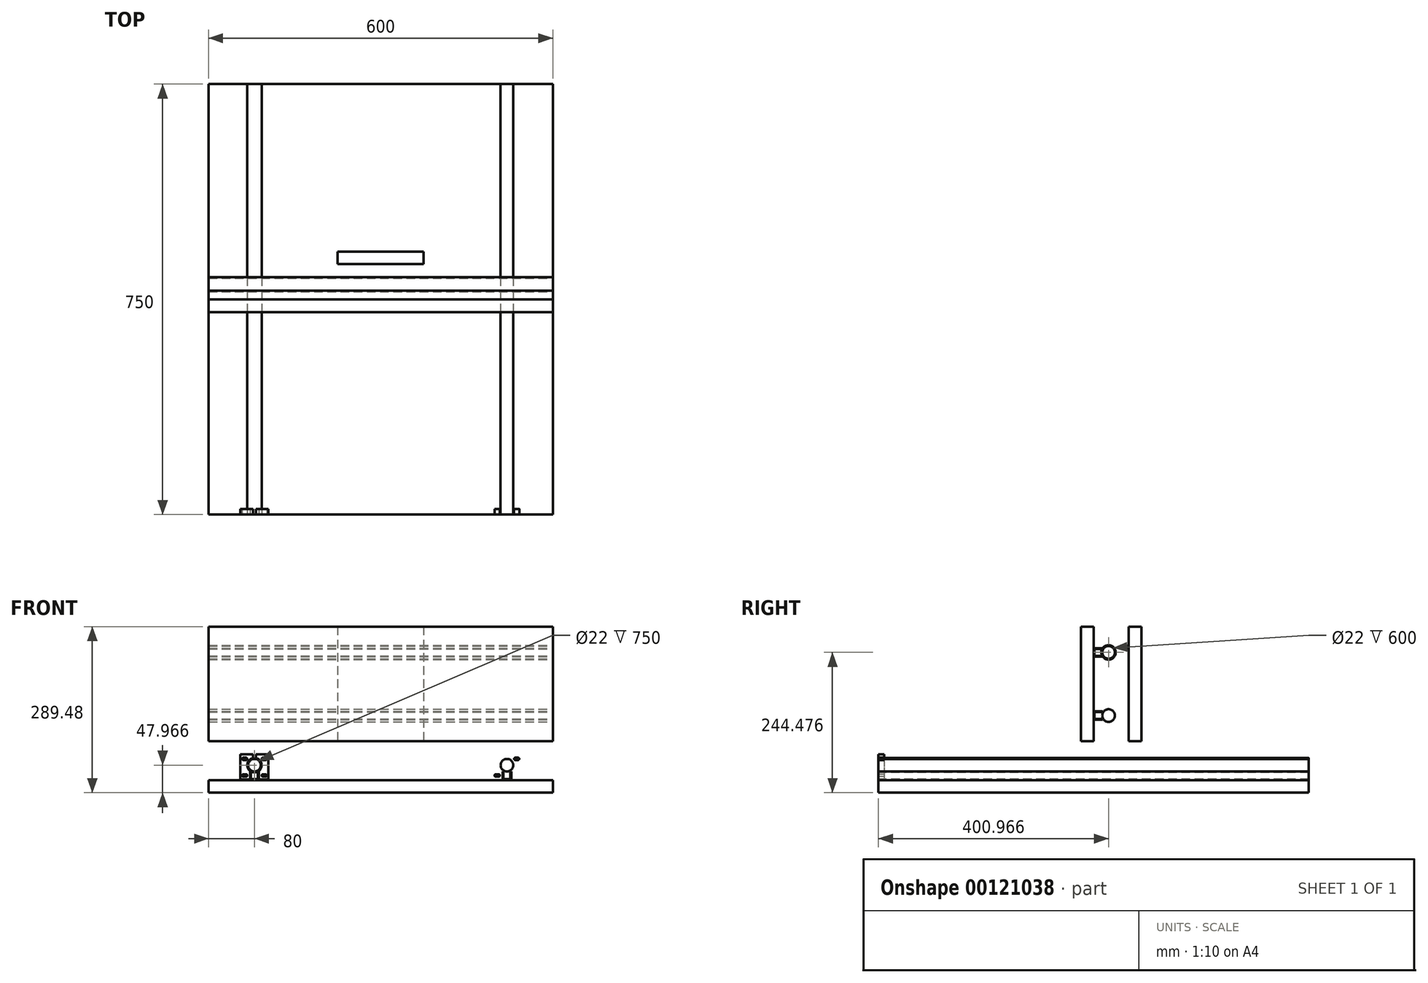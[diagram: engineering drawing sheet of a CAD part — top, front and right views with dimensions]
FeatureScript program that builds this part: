
annotation { "Feature Type Name" : "Feature", "Feature Type Description" : "" }
export const myFeature = defineFeature(function(context is Context, id is Id, definition is map)
    precondition{}
    {
        {
            var Q0;
            Q0=qCreatedBy(makeId("Top.planeOp"),FACE);
            var sketch = newSketch(context, id + "F0", { "sketchPlane" : qUnion([Q0])});
            skLineSegment(sketch, "E0.bottom", {"start": v(-300, 375) * mm, "end": v(300, 375) * mm});
            skLineSegment(sketch, "E0.top", {"start": v(-300, -375) * mm, "end": v(300, -375) * mm});
            skLineSegment(sketch, "E0.left", {"start": v(-300, 375) * mm, "end": v(-300, -375) * mm});
            skLineSegment(sketch, "E0.right", {"start": v(300, 375) * mm, "end": v(300, -375) * mm});
            skSolve(sketch);
        }
        {
            var Q0;
            Q0 = qSketchRegion(id + "F0", true);
            extrude(context, id + "F1", {"entities" : qUnion([Q0]), "depth" : 22 * mm});
        }
        {
            var Q0;
            Q0=makeQuery(id+"F1.opExtrude","SWEPT_FACE",FACE,{"disambiguationData":[OSD([sQuery(id+"F0.wireOp",EDGE,"E0.top")])]});
            var sketch = newSketch(context, id + "F2", { "sketchPlane" : qUnion([Q0])});
            skLineSegment(sketch, "E1", {"start": v(-227.5, 37) * mm, "end": v(-227.5, 22) * mm});
            skLineSegment(sketch, "E2", {"start": v(-227.5, 22) * mm, "end": v(-212.5, 22) * mm});
            skLineSegment(sketch, "E3", {"start": v(-212.5, 22) * mm, "end": v(-212.5, 37) * mm});
            skLineSegment(sketch, "E4", {"start": v(-212.5, 37) * mm, "end": v(-214, 37) * mm});
            skLineSegment(sketch, "E5", {"start": v(-214, 37) * mm, "end": v(-214, 23.5) * mm});
            skLineSegment(sketch, "E6", {"start": v(-214, 23.5) * mm, "end": v(-226, 23.5) * mm});
            skLineSegment(sketch, "E7", {"start": v(-226, 23.5) * mm, "end": v(-226, 37) * mm});
            skLineSegment(sketch, "E8", {"start": v(-226, 37) * mm, "end": v(-227.5, 37) * mm});
            skCircle(sketch, "E9", {"center": v(-220, 47.97) * mm, "radius": 12.5 * mm});
            skCircle(sketch, "E10", {"center": v(-220, 47.97) * mm, "radius": 11 * mm});
            skLineSegment(sketch, "E11.MirrorCS", {"start": v(226, 37) * mm, "end": v(227.5, 37) * mm});
            skLineSegment(sketch, "E12.MirrorCS", {"start": v(212.5, 37) * mm, "end": v(214, 37) * mm});
            skLineSegment(sketch, "E13.MirrorCS", {"start": v(226, 23.5) * mm, "end": v(226, 37) * mm});
            skLineSegment(sketch, "E14.MirrorCS", {"start": v(214, 23.5) * mm, "end": v(226, 23.5) * mm});
            skCircle(sketch, "E15.MirrorC", {"center": v(220, 47.97) * mm, "radius": 12.5 * mm});
            skLineSegment(sketch, "E16.MirrorCS", {"start": v(214, 37) * mm, "end": v(214, 23.5) * mm});
            skCircle(sketch, "E17.MirrorC", {"center": v(220, 47.97) * mm, "radius": 11 * mm});
            skLineSegment(sketch, "E18.MirrorCS", {"start": v(212.5, 22) * mm, "end": v(212.5, 37) * mm});
            skLineSegment(sketch, "E19.MirrorCS", {"start": v(227.5, 22) * mm, "end": v(212.5, 22) * mm});
            skLineSegment(sketch, "E20.MirrorCS", {"start": v(227.5, 37) * mm, "end": v(227.5, 22) * mm});
            skSolve(sketch);
        }
        {
            var Q0;
            Q0=makeQuery(id+"F2.imprint","IMPRINT",FACE,{"disambiguationData":[TD([[makeQuery(id+"F2.imprint","IMPRINT",EDGE,{"derivedFrom":sQuery(id+"F2.wireOp",EDGE,"E1")}),1.0]])]});
            var Q1;
            Q1=makeQuery(id+"F2.imprint","IMPRINT",FACE,{"disambiguationData":[TD([[makeQuery(id+"F2.imprint","IMPRINT",EDGE,{"derivedFrom":sQuery(id+"F2.wireOp",EDGE,"E10")}),-1.0]])]});
            var Q2;
            Q2=makeQuery(id+"F2.imprint","IMPRINT",FACE,{"disambiguationData":[TD([[makeQuery(id+"F2.imprint","IMPRINT",EDGE,{"derivedFrom":sQuery(id+"F2.wireOp",EDGE,"E11.MirrorCS")}),-1.0]])]});
            var Q3;
            Q3=makeQuery(id+"F2.imprint","IMPRINT",FACE,{"disambiguationData":[TD([[makeQuery(id+"F2.imprint","IMPRINT",EDGE,{"derivedFrom":sQuery(id+"F2.wireOp",EDGE,"E17.MirrorC")}),1.0]])]});
            var Q4;
            Q4=makeQuery(id+"F1.opExtrude","SWEPT_FACE",FACE,{"disambiguationData":[OSD([sQuery(id+"F0.wireOp",EDGE,"E0.bottom")])]});
            extrude(context, id + "F3", {"entities" : qUnion([Q0, Q1, Q2, Q3]), "endBound" : BoundingType.UP_TO_SURFACE, "oppositeDirection" : true, "endBoundEntityFace" : qUnion([Q4]), "depth" : 25 * mm});
        }
        {
            var Q0;
            Q0=makeQuery(id+"F1.opExtrude","SWEPT_FACE",FACE,{"disambiguationData":[OSD([sQuery(id+"F0.wireOp",EDGE,"E0.top")])]});
            var sketch = newSketch(context, id + "F4", { "sketchPlane" : qUnion([Q0])});
            skLineSegment(sketch, "E21", {"start": v(-222.5, 60.21) * mm, "end": v(-222.5, 67) * mm});
            skLineSegment(sketch, "E22", {"start": v(-222.5, 67) * mm, "end": v(-244.5, 67) * mm});
            skLineSegment(sketch, "E23", {"start": v(-244.5, 67) * mm, "end": v(-244.5, 22) * mm});
            skLineSegment(sketch, "E24.0", {"start": v(-227.5, 37) * mm, "end": v(-227.5, 22) * mm});
            skLineSegment(sketch, "E25", {"start": v(-244.5, 22) * mm, "end": v(-227.5, 22) * mm, "construction": true});
            skLineSegment(sketch, "E26", {"start": v(-227.5, 37) * mm, "end": v(-227.5, 57.97) * mm});
            skLineSegment(sketch, "E27", {"start": v(-220, 60.47) * mm, "end": v(-220, 22) * mm, "construction": true});
            skLineSegment(sketch, "E28.MirrorCS", {"start": v(-217.5, 60.21) * mm, "end": v(-217.5, 67) * mm});
            skLineSegment(sketch, "E29.MirrorCS", {"start": v(-217.5, 67) * mm, "end": v(-195.5, 67) * mm});
            skLineSegment(sketch, "E30.MirrorCS", {"start": v(-195.5, 67) * mm, "end": v(-195.5, 22) * mm});
            skLineSegment(sketch, "E31.MirrorCS", {"start": v(-195.5, 22) * mm, "end": v(-212.5, 22) * mm, "construction": true});
            skLineSegment(sketch, "E32.MirrorCS", {"start": v(-212.5, 37) * mm, "end": v(-212.5, 22) * mm});
            skLineSegment(sketch, "E33.MirrorCS", {"start": v(-212.5, 37) * mm, "end": v(-212.5, 57.97) * mm});
            skPoint(sketch, "E34.0.center.orphan", {"position": v(-220, 47.97) * mm});
            skArc(sketch, "E35", {"start": v(-239.5, 61) * mm, "mid": v(-241.5, 59) * mm, "end": v(-239.5, 57) * mm});
            skArc(sketch, "E36", {"start": v(-234.5, 57) * mm, "mid": v(-232.5, 59) * mm, "end": v(-234.5, 61) * mm});
            skLineSegment(sketch, "E37", {"start": v(-239.5, 61) * mm, "end": v(-234.5, 61) * mm});
            skLineSegment(sketch, "E38", {"start": v(-239.5, 57) * mm, "end": v(-234.5, 57) * mm});
            skCircle(sketch, "E39.0", {"center": v(-220, 47.97) * mm, "radius": 12.5 * mm});
            skLineSegment(sketch, "E40", {"start": v(-244.5, 44.5) * mm, "end": v(-195.5, 44.5) * mm, "construction": true});
            skLineSegment(sketch, "E41.MirrorCS", {"start": v(-239.5, 28) * mm, "end": v(-234.5, 28) * mm});
            skLineSegment(sketch, "E42.MirrorCS", {"start": v(-239.5, 32) * mm, "end": v(-234.5, 32) * mm});
            skArc(sketch, "E43.MirrorCS", {"start": v(-239.5, 28) * mm, "mid": v(-241.5, 30) * mm, "end": v(-239.5, 32) * mm});
            skArc(sketch, "E44.MirrorCS", {"start": v(-234.5, 32) * mm, "mid": v(-232.5, 30) * mm, "end": v(-234.5, 28) * mm});
            skLineSegment(sketch, "E45.MirrorCS", {"start": v(-200.5, 57) * mm, "end": v(-205.5, 57) * mm});
            skArc(sketch, "E46.MirrorCS", {"start": v(-200.5, 61) * mm, "mid": v(-198.5, 59) * mm, "end": v(-200.5, 57) * mm});
            skArc(sketch, "E47.MirrorCS", {"start": v(-205.5, 57) * mm, "mid": v(-207.5, 59) * mm, "end": v(-205.5, 61) * mm});
            skLineSegment(sketch, "E48.MirrorCS", {"start": v(-200.5, 61) * mm, "end": v(-205.5, 61) * mm});
            skLineSegment(sketch, "E49.MirrorCS", {"start": v(-200.5, 32) * mm, "end": v(-205.5, 32) * mm});
            skLineSegment(sketch, "E50.MirrorCS", {"start": v(-200.5, 28) * mm, "end": v(-205.5, 28) * mm});
            skArc(sketch, "E51.MirrorCS", {"start": v(-205.5, 32) * mm, "mid": v(-207.5, 30) * mm, "end": v(-205.5, 28) * mm});
            skArc(sketch, "E52.MirrorCS", {"start": v(-200.5, 28) * mm, "mid": v(-198.5, 30) * mm, "end": v(-200.5, 32) * mm});
            skArc(sketch, "E53.MirrorCS", {"start": v(234.5, 57) * mm, "mid": v(232.5, 59) * mm, "end": v(234.5, 61) * mm});
            skArc(sketch, "E54.MirrorCS", {"start": v(239.5, 61) * mm, "mid": v(241.5, 59) * mm, "end": v(239.5, 57) * mm});
            skLineSegment(sketch, "E55.MirrorCS", {"start": v(239.5, 57) * mm, "end": v(234.5, 57) * mm});
            skArc(sketch, "E56.MirrorCS", {"start": v(200.5, 28) * mm, "mid": v(198.5, 30) * mm, "end": v(200.5, 32) * mm});
            skLineSegment(sketch, "E57.MirrorCS", {"start": v(200.5, 28) * mm, "end": v(205.5, 28) * mm});
            skLineSegment(sketch, "E58.MirrorCS", {"start": v(239.5, 61) * mm, "end": v(234.5, 61) * mm});
            skLineSegment(sketch, "E59.MirrorCS", {"start": v(200.5, 32) * mm, "end": v(205.5, 32) * mm});
            skArc(sketch, "E60.MirrorCS", {"start": v(205.5, 32) * mm, "mid": v(207.5, 30) * mm, "end": v(205.5, 28) * mm});
            skArc(sketch, "E61.MirrorCS", {"start": v(239.5, 28) * mm, "mid": v(241.5, 30) * mm, "end": v(239.5, 32) * mm});
            skLineSegment(sketch, "E62.MirrorCS", {"start": v(200.5, 61) * mm, "end": v(205.5, 61) * mm});
            skArc(sketch, "E63.MirrorCS", {"start": v(205.5, 57) * mm, "mid": v(207.5, 59) * mm, "end": v(205.5, 61) * mm});
            skLineSegment(sketch, "E64.MirrorCS", {"start": v(217.5, 60.21) * mm, "end": v(217.5, 67) * mm});
            skLineSegment(sketch, "E65.MirrorCS", {"start": v(212.5, 37) * mm, "end": v(212.5, 57.97) * mm});
            skArc(sketch, "E66.MirrorCS", {"start": v(200.5, 61) * mm, "mid": v(198.5, 59) * mm, "end": v(200.5, 57) * mm});
            skLineSegment(sketch, "E67.MirrorCS", {"start": v(222.5, 60.21) * mm, "end": v(222.5, 67) * mm});
            skLineSegment(sketch, "E68.MirrorCS", {"start": v(239.5, 28) * mm, "end": v(234.5, 28) * mm});
            skLineSegment(sketch, "E69.MirrorCS", {"start": v(200.5, 57) * mm, "end": v(205.5, 57) * mm});
            skLineSegment(sketch, "E70.MirrorCS", {"start": v(239.5, 32) * mm, "end": v(234.5, 32) * mm});
            skLineSegment(sketch, "E71.MirrorCS", {"start": v(227.5, 37) * mm, "end": v(227.5, 57.97) * mm});
            skArc(sketch, "E72.MirrorCS", {"start": v(234.5, 32) * mm, "mid": v(232.5, 30) * mm, "end": v(234.5, 28) * mm});
            skLineSegment(sketch, "E73.MirrorCS", {"start": v(217.5, 67) * mm, "end": v(195.5, 67) * mm});
            skLineSegment(sketch, "E74.MirrorCS", {"start": v(195.5, 67) * mm, "end": v(195.5, 22) * mm});
            skLineSegment(sketch, "E75.MirrorCS", {"start": v(244.5, 44.5) * mm, "end": v(195.5, 44.5) * mm, "construction": true});
            skLineSegment(sketch, "E76.MirrorCS", {"start": v(195.5, 22) * mm, "end": v(212.5, 22) * mm});
            skCircle(sketch, "E77.MirrorC", {"center": v(220, 47.97) * mm, "radius": 12.5 * mm});
            skLineSegment(sketch, "E78.MirrorCS", {"start": v(212.5, 37) * mm, "end": v(212.5, 22) * mm});
            skLineSegment(sketch, "E79.MirrorCS", {"start": v(220, 60.47) * mm, "end": v(220, 22) * mm, "construction": true});
            skLineSegment(sketch, "E80.MirrorCS", {"start": v(222.5, 67) * mm, "end": v(244.5, 67) * mm});
            skLineSegment(sketch, "E81.MirrorCS", {"start": v(244.5, 67) * mm, "end": v(244.5, 22) * mm});
            skLineSegment(sketch, "E82.MirrorCS", {"start": v(227.5, 37) * mm, "end": v(227.5, 22) * mm});
            skLineSegment(sketch, "E83.MirrorCS", {"start": v(244.5, 22) * mm, "end": v(227.5, 22) * mm});
            skLineSegment(sketch, "E84", {"start": v(-244.5, 23) * mm, "end": v(-227.5, 23) * mm});
            skLineSegment(sketch, "E85.MirrorCS", {"start": v(-195.5, 23) * mm, "end": v(-212.5, 23) * mm});
            skLineSegment(sketch, "E86.MirrorCS", {"start": v(244.5, 22) * mm, "end": v(227.5, 22) * mm, "construction": true});
            skLineSegment(sketch, "E87.MirrorCS", {"start": v(195.5, 22) * mm, "end": v(212.5, 22) * mm, "construction": true});
            skLineSegment(sketch, "E88.MirrorCS", {"start": v(244.5, 23) * mm, "end": v(227.5, 23) * mm});
            skLineSegment(sketch, "E89.MirrorCS", {"start": v(195.5, 23) * mm, "end": v(212.5, 23) * mm});
            skSolve(sketch);
        }
        {
            var Q0;
            {var subQ1=sQuery(id+"F4.wireOp",EDGE,"E21");Q0=makeQuery(id+"F4.imprint","IMPRINT",FACE,{"disambiguationData":[TD([[makeQuery(id+"F4.imprint","IMPRINT",EDGE,{"derivedFrom":subQ1}),1.0]])]});}
            var Q1;
            {var subQ1=sQuery(id+"F4.wireOp",EDGE,"E28.MirrorCS");Q1=makeQuery(id+"F4.imprint","IMPRINT",FACE,{"disambiguationData":[TD([[makeQuery(id+"F4.imprint","IMPRINT",EDGE,{"derivedFrom":subQ1}),-1.0]])]});}
            var Q2;
            Q2=makeQuery(id+"F4.imprint","IMPRINT",FACE,{"disambiguationData":[TD([[makeQuery(id+"F4.imprint","IMPRINT",EDGE,{"derivedFrom":sQuery(id+"F4.wireOp",EDGE,"E56.MirrorCS")}),1.0]])]});
            var Q3;
            Q3=makeQuery(id+"F4.imprint","IMPRINT",FACE,{"disambiguationData":[TD([[makeQuery(id+"F4.imprint","IMPRINT",EDGE,{"derivedFrom":sQuery(id+"F4.wireOp",EDGE,"E53.MirrorCS")}),1.0]])]});
            extrude(context, id + "F5", {"entities" : qUnion([Q0, Q1, Q2, Q3]), "oppositeDirection" : true, "depth" : 10 * mm});
        }
        {
            var Q0;
            Q0=qCreatedBy(makeId("Front.planeOp"),FACE);
            var sketch = newSketch(context, id + "F6", { "sketchPlane" : qUnion([Q0])});
            skLineSegment(sketch, "E90.bottom", {"start": v(-300, 289.48) * mm, "end": v(300, 289.48) * mm});
            skLineSegment(sketch, "E90.top", {"start": v(-300, 89.48) * mm, "end": v(300, 89.48) * mm});
            skLineSegment(sketch, "E90.left", {"start": v(-300, 289.48) * mm, "end": v(-300, 89.48) * mm});
            skLineSegment(sketch, "E90.right", {"start": v(300, 289.48) * mm, "end": v(300, 89.48) * mm});
            skSolve(sketch);
        }
        {
            var Q0;
            Q0 = qSketchRegion(id + "F6", true);
            extrude(context, id + "F7", {"entities" : qUnion([Q0]), "depth" : 22 * mm});
        }
        {
            var Q0;
            Q0=makeQuery(id+"F7.opExtrude","SWEPT_FACE",FACE,{"disambiguationData":[OSD([sQuery(id+"F6.wireOp",EDGE,"E90.right")])]});
            var sketch = newSketch(context, id + "F8", { "sketchPlane" : qUnion([Q0])});
            skLineSegment(sketch, "E91", {"start": v(-22, 244.48) * mm, "end": v(279.76, 244.48) * mm, "construction": true});
            skLineSegment(sketch, "E92", {"start": v(-22, 189.48) * mm, "end": v(0, 189.48) * mm, "construction": true});
            skLineSegment(sketch, "E93", {"start": v(0, 244.48) * mm, "end": v(0, 251.98) * mm});
            skLineSegment(sketch, "E94", {"start": v(0, 251.98) * mm, "end": v(15, 251.98) * mm});
            skLineSegment(sketch, "E95", {"start": v(15, 251.98) * mm, "end": v(15, 250.48) * mm});
            skLineSegment(sketch, "E96", {"start": v(15, 250.48) * mm, "end": v(1.5, 250.48) * mm});
            skLineSegment(sketch, "E97", {"start": v(1.5, 250.48) * mm, "end": v(1.5, 244.48) * mm});
            skLineSegment(sketch, "E98.MirrorCS", {"start": v(15, 236.98) * mm, "end": v(15, 238.48) * mm});
            skLineSegment(sketch, "E99.MirrorCS", {"start": v(0, 244.48) * mm, "end": v(0, 236.98) * mm});
            skLineSegment(sketch, "E100.MirrorCS", {"start": v(0, 236.98) * mm, "end": v(15, 236.98) * mm});
            skLineSegment(sketch, "E101.MirrorCS", {"start": v(15, 238.48) * mm, "end": v(1.5, 238.48) * mm});
            skLineSegment(sketch, "E102.MirrorCS", {"start": v(1.5, 238.48) * mm, "end": v(1.5, 244.48) * mm});
            skCircle(sketch, "E103", {"center": v(25.97, 244.48) * mm, "radius": 12.5 * mm});
            skCircle(sketch, "E104", {"center": v(25.97, 244.48) * mm, "radius": 11 * mm});
            skLineSegment(sketch, "E105.MirrorCS", {"start": v(15, 141.98) * mm, "end": v(15, 140.48) * mm});
            skLineSegment(sketch, "E106.MirrorCS", {"start": v(15, 126.98) * mm, "end": v(15, 128.48) * mm});
            skLineSegment(sketch, "E107.MirrorCS", {"start": v(0, 134.48) * mm, "end": v(0, 141.98) * mm});
            skLineSegment(sketch, "E108.MirrorCS", {"start": v(0, 141.98) * mm, "end": v(15, 141.98) * mm});
            skCircle(sketch, "E109.MirrorC", {"center": v(25.97, 134.48) * mm, "radius": 11 * mm});
            skLineSegment(sketch, "E110.MirrorCS", {"start": v(1.5, 140.48) * mm, "end": v(1.5, 134.48) * mm});
            skLineSegment(sketch, "E111.MirrorCS", {"start": v(0, 134.48) * mm, "end": v(0, 126.98) * mm});
            skLineSegment(sketch, "E112.MirrorCS", {"start": v(15, 140.48) * mm, "end": v(1.5, 140.48) * mm});
            skLineSegment(sketch, "E113.MirrorCS", {"start": v(1.5, 128.48) * mm, "end": v(1.5, 134.48) * mm});
            skLineSegment(sketch, "E114.MirrorCS", {"start": v(0, 126.98) * mm, "end": v(15, 126.98) * mm});
            skLineSegment(sketch, "E115.MirrorCS", {"start": v(15, 128.48) * mm, "end": v(1.5, 128.48) * mm});
            skCircle(sketch, "E116.MirrorC", {"center": v(25.97, 134.48) * mm, "radius": 12.5 * mm});
            skSolve(sketch);
        }
        {
            var Q0;
            Q0=makeQuery(id+"F8.imprint","IMPRINT",FACE,{"disambiguationData":[TD([[makeQuery(id+"F8.imprint","IMPRINT",EDGE,{"derivedFrom":sQuery(id+"F8.wireOp",EDGE,"E104")}),-1.0]])]});
            var Q1;
            Q1=makeQuery(id+"F8.imprint","IMPRINT",FACE,{"disambiguationData":[TD([[makeQuery(id+"F8.imprint","IMPRINT",EDGE,{"derivedFrom":sQuery(id+"F8.wireOp",EDGE,"E93")}),1.0]])]});
            var Q2;
            Q2=makeQuery(id+"F8.imprint","IMPRINT",FACE,{"disambiguationData":[TD([[makeQuery(id+"F8.imprint","IMPRINT",EDGE,{"derivedFrom":sQuery(id+"F8.wireOp",EDGE,"E105.MirrorCS")}),-1.0]])]});
            var Q3;
            Q3=makeQuery(id+"F8.imprint","IMPRINT",FACE,{"disambiguationData":[TD([[makeQuery(id+"F8.imprint","IMPRINT",EDGE,{"derivedFrom":sQuery(id+"F8.wireOp",EDGE,"E109.MirrorC")}),1.0]])]});
            var Q4;
            Q4=makeQuery(id+"F7.opExtrude","SWEPT_FACE",FACE,{"disambiguationData":[OSD([sQuery(id+"F6.wireOp",EDGE,"E90.left")])]});
            extrude(context, id + "F9", {"entities" : qUnion([Q0, Q1, Q2, Q3]), "endBound" : BoundingType.UP_TO_SURFACE, "oppositeDirection" : true, "endBoundEntityFace" : qUnion([Q4]), "depth" : 25 * mm});
        }
        {
            var Q0;
            Q0=qCreatedBy(makeId("Right.planeOp"),FACE);
            var sketch = newSketch(context, id + "F10", { "sketchPlane" : qUnion([Q0])});
            skLineSegment(sketch, "E117.0.0", {"start": v(0, 89.48) * mm, "end": v(0, 289.48) * mm, "construction": true});
            skLineSegment(sketch, "E117.0.1", {"start": v(0, 289.48) * mm, "end": v(-22, 289.48) * mm, "construction": true});
            skLineSegment(sketch, "E117.0.2", {"start": v(-22, 289.48) * mm, "end": v(-22, 89.48) * mm, "construction": true});
            skLineSegment(sketch, "E117.0.3", {"start": v(-22, 89.48) * mm, "end": v(0, 89.48) * mm, "construction": true});
            skLineSegment(sketch, "E118.bottom", {"start": v(61.22, 289.48) * mm, "end": v(83.22, 289.48) * mm});
            skLineSegment(sketch, "E118.top", {"start": v(61.22, 89.48) * mm, "end": v(83.22, 89.48) * mm});
            skLineSegment(sketch, "E118.left", {"start": v(61.22, 289.48) * mm, "end": v(61.22, 89.48) * mm});
            skLineSegment(sketch, "E118.right", {"start": v(83.22, 289.48) * mm, "end": v(83.22, 89.48) * mm});
            skCircle(sketch, "E119.0", {"center": v(25.97, 244.48) * mm, "radius": 11 * mm, "construction": true});
            skSolve(sketch);
        }
        {
            var Q0;
            Q0 = qSketchRegion(id + "F10", true);
            extrude(context, id + "F11", {"entities" : qUnion([Q0]), "endBound" : BoundingType.SYMMETRIC, "depth" : 150 * mm});
        }
    });
